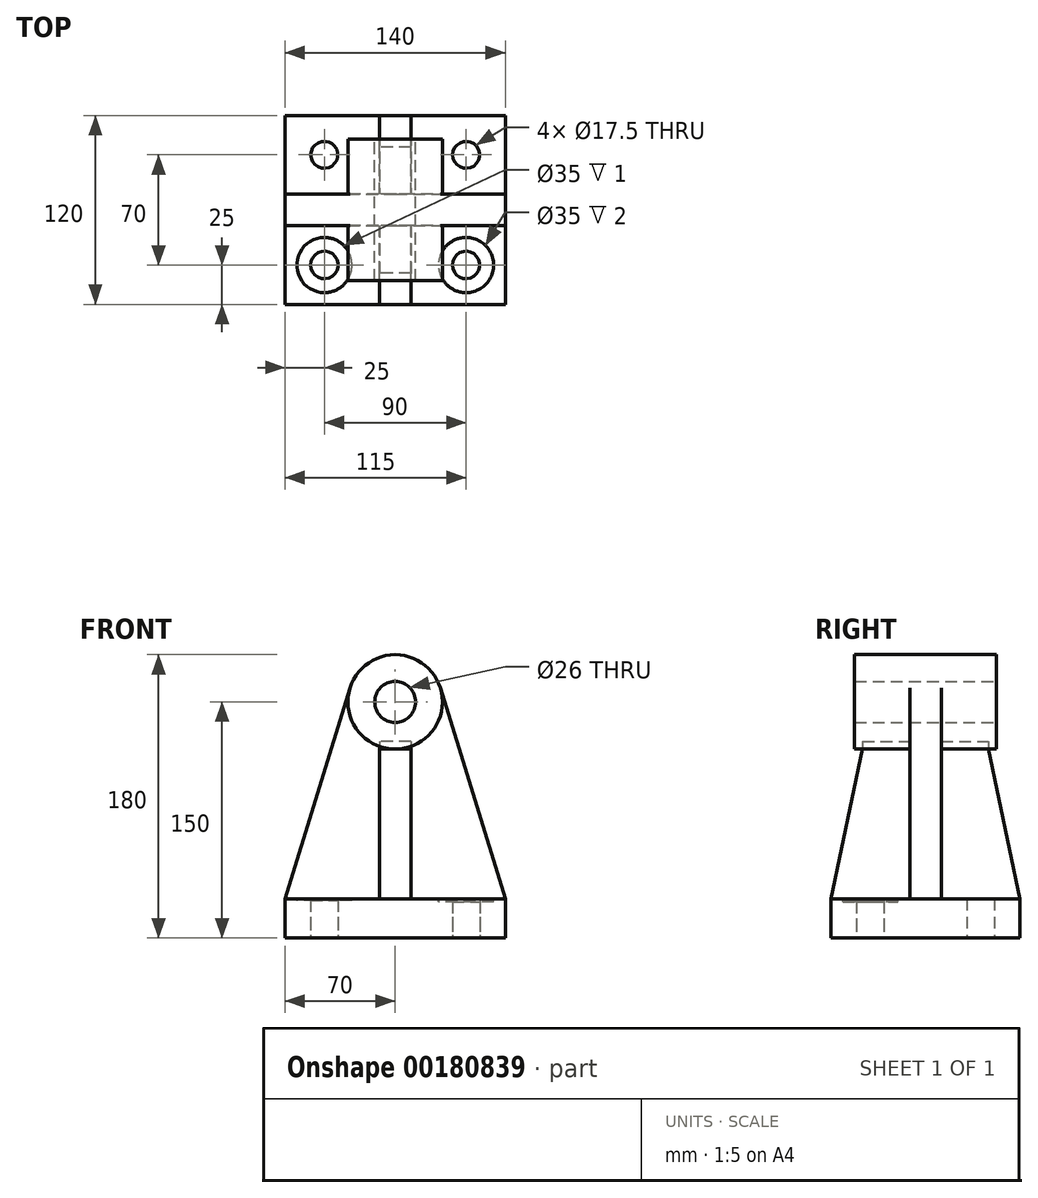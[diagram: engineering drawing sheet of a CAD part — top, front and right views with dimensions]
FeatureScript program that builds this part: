
annotation { "Feature Type Name" : "Feature", "Feature Type Description" : "" }
export const myFeature = defineFeature(function(context is Context, id is Id, definition is map)
    precondition{}
    {
        {
            var Q0;
            Q0=qCreatedBy(makeId("Front.planeOp"),FACE);
            var sketch = newSketch(context, id + "F0", { "sketchPlane" : qUnion([Q0])});
            skLineSegment(sketch, "E0", {"start": v(0, 0) * mm, "end": v(-70, 0) * mm});
            skLineSegment(sketch, "E1", {"start": v(-70, 0) * mm, "end": v(-70, 25) * mm});
            skCircle(sketch, "E2", {"center": v(0, 150) * mm, "radius": 30 * mm});
            skLineSegment(sketch, "E3", {"start": v(-28.66, 158.85) * mm, "end": v(-70, 25) * mm});
            skLineSegment(sketch, "E4", {"start": v(0, 0) * mm, "end": v(70, 0) * mm});
            skLineSegment(sketch, "E5", {"start": v(70, 0) * mm, "end": v(70, 25) * mm});
            skLineSegment(sketch, "E6", {"start": v(70, 25) * mm, "end": v(28.66, 158.85) * mm});
            skLineSegment(sketch, "E7", {"start": v(-70, 25) * mm, "end": v(70, 25) * mm});
            skCircle(sketch, "E8", {"center": v(0, 150) * mm, "radius": 12.5 * mm});
            skSolve(sketch);
        }
        {
            var Q0;
            {var subQ0=sQuery(id+"F0.wireOp",EDGE,"E3");Q0=makeQuery(id+"F0.imprint","IMPRINT",FACE,{"disambiguationData":[TD([[makeQuery(id+"F0.imprint","IMPRINT",EDGE,{"derivedFrom":subQ0}),1.0]])]});}
            extrude(context, id + "F1", {"entities" : qUnion([Q0]), "endBound" : BoundingType.SYMMETRIC, "depth" : 20 * mm});
        }
        {
            var Q0;
            Q0=qCreatedBy(makeId("Front.planeOp"),FACE);
            var sketch = newSketch(context, id + "F2", { "sketchPlane" : qUnion([Q0])});
            skLineSegment(sketch, "E9", {"start": v(70, 25.04) * mm, "end": v(70, 0) * mm});
            skLineSegment(sketch, "E10", {"start": v(70, 0) * mm, "end": v(-70, 0) * mm});
            skLineSegment(sketch, "E11", {"start": v(-70, 0) * mm, "end": v(-70, 25) * mm});
            skLineSegment(sketch, "E12", {"start": v(-70, 25) * mm, "end": v(70, 25.04) * mm});
            skSolve(sketch);
        }
        {
            var Q0;
            Q0 = qSketchRegion(id + "F2", true);
            extrude(context, id + "F3", {"entities" : qUnion([Q0]), "operationType" : NewBodyOperationType.ADD, "endBound" : BoundingType.SYMMETRIC, "depth" : 120 * mm});
        }
        {
            var Q0;
            Q0=qCreatedBy(makeId("Front.planeOp"),FACE);
            var sketch = newSketch(context, id + "F4", { "sketchPlane" : qUnion([Q0])});
            skCircle(sketch, "E13", {"center": v(0, 150) * mm, "radius": 30 * mm});
            skCircle(sketch, "E14", {"center": v(0, 150) * mm, "radius": 13 * mm});
            skSolve(sketch);
        }
        {
            var Q0;
            Q0=makeQuery(id+"F4.imprint","IMPRINT",FACE,{"disambiguationData":[TD([[makeQuery(id+"F4.imprint","IMPRINT",EDGE,{"derivedFrom":sQuery(id+"F4.wireOp",EDGE,"E13")}),1.0]])]});
            extrude(context, id + "F5", {"entities" : qUnion([Q0]), "operationType" : NewBodyOperationType.ADD, "endBound" : BoundingType.SYMMETRIC, "depth" : 90 * mm});
        }
        {
            var Q0;
            Q0=qCreatedBy(makeId("Right.planeOp"),FACE);
            var sketch = newSketch(context, id + "F6", { "sketchPlane" : qUnion([Q0])});
            skLineSegment(sketch, "E15", {"start": v(40, 120) * mm, "end": v(60, 25) * mm});
            skLineSegment(sketch, "E16", {"start": v(60, 25) * mm, "end": v(10, 25) * mm});
            skLineSegment(sketch, "E17", {"start": v(10, 25) * mm, "end": v(10, 120) * mm});
            skLineSegment(sketch, "E18", {"start": v(10, 120) * mm, "end": v(40, 120) * mm});
            skLineSegment(sketch, "E19", {"start": v(-60, 25) * mm, "end": v(-40, 120) * mm});
            skLineSegment(sketch, "E20", {"start": v(-40, 120) * mm, "end": v(-10.03, 120) * mm});
            skLineSegment(sketch, "E21", {"start": v(-10.03, 120) * mm, "end": v(-10.03, 25) * mm});
            skLineSegment(sketch, "E22", {"start": v(-10.03, 25) * mm, "end": v(-60, 25) * mm});
            skSolve(sketch);
        }
        {
            var Q0;
            Q0=makeQuery(id+"F6.imprint","IMPRINT",FACE,{"disambiguationData":[TD([[makeQuery(id+"F6.imprint","IMPRINT",EDGE,{"derivedFrom":sQuery(id+"F6.wireOp",EDGE,"E15")}),-1.0]])]});
            extrude(context, id + "F7", {"entities" : qUnion([Q0]), "endBound" : BoundingType.SYMMETRIC, "depth" : 20 * mm});
        }
        {
            var Q0;
            Q0 = qSketchRegion(id + "F6", true);
            extrude(context, id + "F8", {"entities" : qUnion([Q0]), "endBound" : BoundingType.SYMMETRIC, "depth" : 20 * mm});
        }
        {
            var Q0;
            Q0=makeQuery(id+"F7.opExtrude","SWEPT_FACE",FACE,{"disambiguationData":[OSD([sQuery(id+"F6.wireOp",EDGE,"E18")])]});
            extrude(context, id + "F9", {"entities" : qUnion([Q0]), "depth" : 5 * mm});
        }
        {
            var Q0;
            Q0=makeQuery(id+"F8.opExtrude","SWEPT_FACE",FACE,{"disambiguationData":[OSD([sQuery(id+"F6.wireOp",EDGE,"E20")])]});
            extrude(context, id + "F10", {"entities" : qUnion([Q0]), "depth" : 5 * mm});
        }
        {
            var Q0;
            Q0=makeQuery(id+"F3.opExtrude","SWEPT_FACE",FACE,{"disambiguationData":[OSD([sQuery(id+"F2.wireOp",EDGE,"E10")])]});
            var sketch = newSketch(context, id + "F11", { "sketchPlane" : qUnion([Q0])});
            skCircle(sketch, "E23", {"center": v(-45, -35) * mm, "radius": 8.75 * mm});
            skCircle(sketch, "E24.0.1.0", {"center": v(-45, 35) * mm, "radius": 8.75 * mm});
            skCircle(sketch, "E24.1.0.0", {"center": v(45, -35) * mm, "radius": 8.75 * mm});
            skCircle(sketch, "E24.1.1.0", {"center": v(45, 35) * mm, "radius": 8.75 * mm});
            skLineSegment(sketch, "E24.direction1", {"start": v(-45, -35) * mm, "end": v(45, -35) * mm, "construction": true});
            skLineSegment(sketch, "E24.direction2", {"start": v(-45, -35) * mm, "end": v(-45, 35) * mm, "construction": true});
            skSolve(sketch);
        }
        {
            var Q0;
            Q0 = qSketchRegion(id + "F11", true);
            extrude(context, id + "F12", {"entities" : qUnion([Q0]), "operationType" : NewBodyOperationType.REMOVE, "oppositeDirection" : true, "depth" : 50 * mm});
        }
        {
            var Q0;
            Q0=makeQuery(id+"F3.opExtrude","SWEPT_FACE",FACE,{"disambiguationData":[OSD([sQuery(id+"F2.wireOp",EDGE,"E12")])]});
            var sketch = newSketch(context, id + "F13", { "sketchPlane" : qUnion([Q0])});
            skCircle(sketch, "E25", {"center": v(-45, -35) * mm, "radius": 17.5 * mm});
            skSolve(sketch);
        }
        {
            var Q0;
            Q0=makeQuery(id+"F13.imprint","IMPRINT",FACE,{"disambiguationData":[TD([[makeQuery(id+"F13.imprint","IMPRINT",EDGE,{"derivedFrom":sQuery(id+"F13.wireOp",EDGE,"E25")}),1.0]])]});
            extrude(context, id + "F14", {"entities" : qUnion([Q0]), "operationType" : NewBodyOperationType.REMOVE, "oppositeDirection" : true, "depth" : 1 * mm});
        }
        {
            var Q0;
            Q0=makeQuery(id+"F3.opExtrude","SWEPT_FACE",FACE,{"disambiguationData":[OSD([sQuery(id+"F2.wireOp",EDGE,"E12")])]});
            var sketch = newSketch(context, id + "F15", { "sketchPlane" : qUnion([Q0])});
            skCircle(sketch, "E26", {"center": v(45, -35) * mm, "radius": 17.5 * mm});
            skSolve(sketch);
        }
        {
            var Q0;
            Q0=makeQuery(id+"F15.imprint","IMPRINT",FACE,{"disambiguationData":[TD([[makeQuery(id+"F15.imprint","IMPRINT",EDGE,{"derivedFrom":sQuery(id+"F15.wireOp",EDGE,"E26")}),1.0]])]});
            extrude(context, id + "F16", {"entities" : qUnion([Q0]), "operationType" : NewBodyOperationType.REMOVE, "oppositeDirection" : true, "depth" : 2 * mm});
        }
    });
